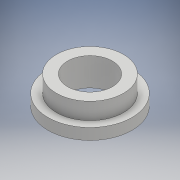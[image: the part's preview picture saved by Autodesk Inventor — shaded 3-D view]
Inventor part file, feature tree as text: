
AUTODESK INVENTOR PART (.ipt)
format: ipt  version: 2018 (Build 220112000, 112)  size: 111,616 bytes
history: native  units: mm
features: extrude x3, sketch x3
ambient origin geometry x8: Origin, YZ Plane, XZ Plane, XY Plane, X Axis, Y Axis, Z Axis, Center Point
bodies: Solid1 (feature_tree)
feature tree (6):
  extrude  "Extrusion1"  Depth=2.0mm TaperAngle=0.0deg
  extrude  "Extrusion2"  Depth=3.0mm TaperAngle=0.0deg
  extrude  "Extrusion3"  Depth=3.0mm TaperAngle=0.0deg
  sketch  "Sketch1"  dims[d0=15.0mm d1=2.0mm d2=0.0mm]
  sketch  "Sketch2"  dims[d3=12.0mm d4=3.0mm d5=0.0mm]
  sketch  "Sketch3"  dims[d6=8.0mm d7=3.0mm d8=0.0mm]
